# Revit family: Berica 1.0 M
name_source: partatom
category: Lighting Fixtures
units: mm (PartAtom-declared; Revit-internal decimal feet)

## family parameters
Always vertical = No
Cut with Voids When Loaded = No
Light Source = No
OmniClass Number = 23.80.70.00
OmniClass Title = Lighting
Part Type = Normal
Room Calculation Point = Yes
Round Connector Dimension = Use Diameter
Shared = No
Work Plane-Based = Yes

## types (4) — shared parameters
Apparent Load Phase 1 = 5 W
Body = L&L_Anticorodal aluminium
CRI = CRI >90
Code = -
Control system = ON/OFF
Cutout dimensions = -
Default Elevation = 1219 mm
Delivered lumen output = 328 lm (3000K, 43°x96°) per beam
Description = Wall mounted for indoor applications, double beam
Energy efficiency class = A A+ A++
Features = -
Height mm = 120 mm
Horizontal rotation max = 0.00°
IP = IP40
LED Colour = 3000K
Length mm = 120 mm
Lumen output at source = 410 lm (3000K) per beam
Manufacturer = L&L Luce&Light
Material = body and cover in anticorodal aluminium
Model = Berica 1.0
Mounting = surface mounted (wall)
No. and type of led = 16 mid power LEDs, 3-step MacAdam, 50 000h L80 B10 (Ta 25°C)
Notes = -
Power = 8W
Power cables = -
Power supply = 230Vac
Power supply unit = built-in
not included
not included
URL = https://www.lucelight.it
URL Accessories and power supply units = https://www.lucelight.it
URL DXF = https://www.lucelight.it
URL Description = https://www.lucelight.it
URL General code = https://www.lucelight.it
URL IES Photometric file = https://www.lucelight.it
URL Image = https://www.lucelight.it
Vertical rotation max = 0.00°
Weight kg = 0.35 kg
Width mm = 33 mm
Wiring = -

## per-type parameters (varying)
| type | Optics | light Source |
| Berica 1.0 L 43°x96° | 43°x96° | Light Source Berica 1.0 : L 43°x96° |
| Berica 1.0 K 54°x90° | 54°x90° | Light Source Berica 1.0 : K 54°x90° |
| Berica 1.0 diffuse | diffuse | Light Source Berica 1.0 : diffuse |
| Berica 1.0 asymmetrical | asymmetrical | Light Source Berica 1.0 : asymmetrical |

## geometry (parser evidence)
native form markers: Blend x6, Sweep x7
no freeform markers — native parametric forms only
